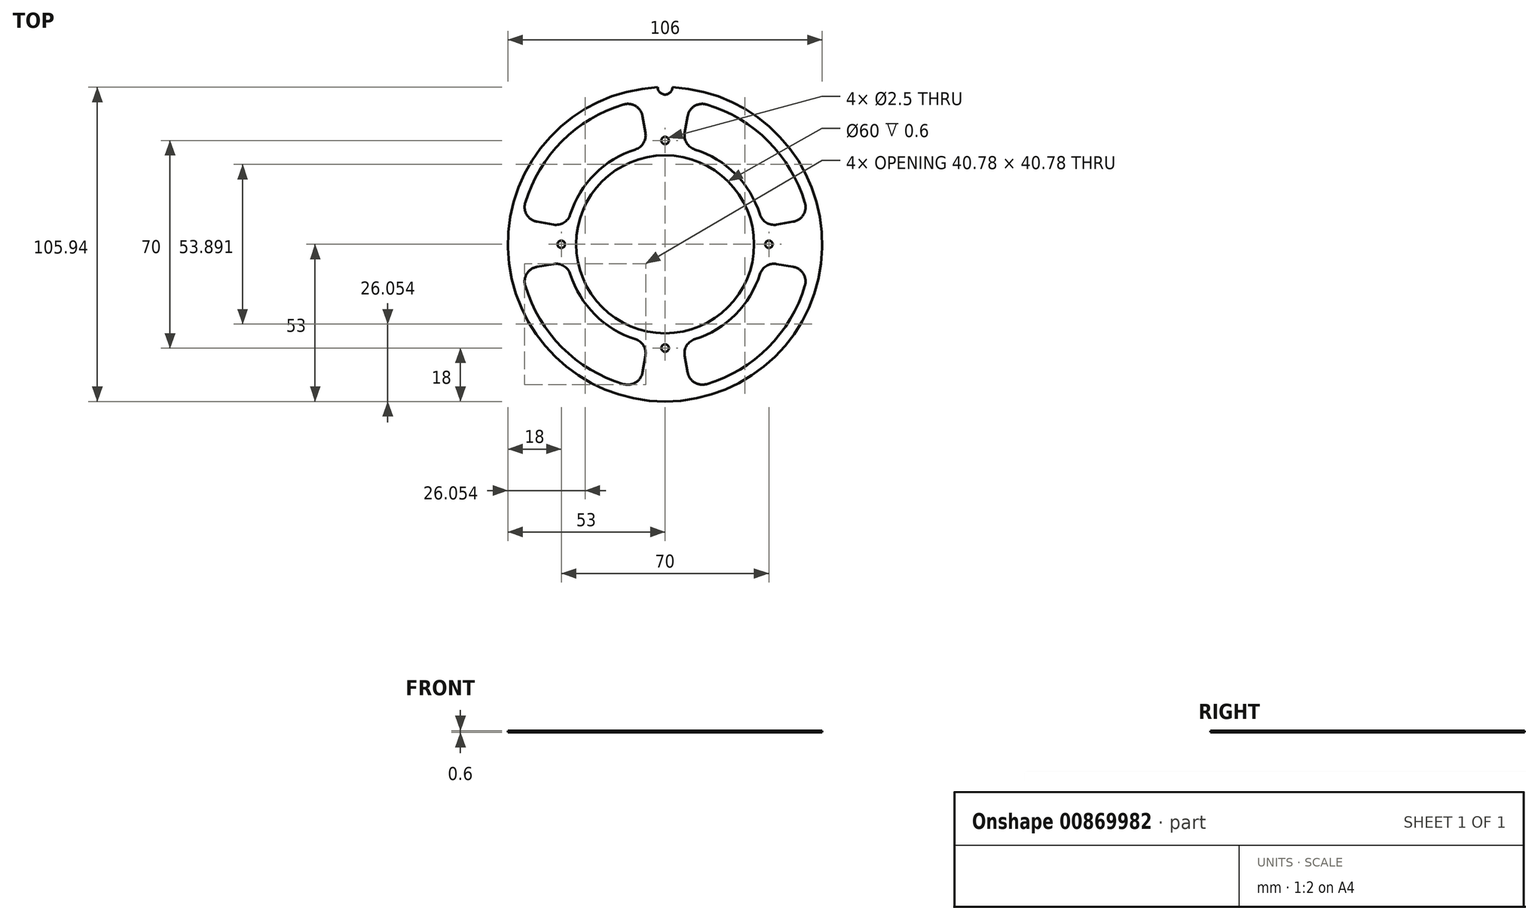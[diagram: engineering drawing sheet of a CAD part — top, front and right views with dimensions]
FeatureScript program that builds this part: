
annotation { "Feature Type Name" : "Feature", "Feature Type Description" : "" }
export const myFeature = defineFeature(function(context is Context, id is Id, definition is map)
    precondition{}
    {
        {
            var Q0;
            Q0=qCreatedBy(makeId("Top.planeOp"),FACE);
            var sketch = newSketch(context, id + "F0", { "sketchPlane" : qUnion([Q0])});
            skCircle(sketch, "E0", {"center": v(0, 0) * mm, "radius": 30 * mm});
            skCircle(sketch, "E1", {"center": v(0, 0) * mm, "radius": 53 * mm});
            skSolve(sketch);
        }
        {
            var Q0;
            Q0=makeQuery(id+"F0.imprint","IMPRINT",FACE,{"disambiguationData":[TD([[makeQuery(id+"F0.imprint","IMPRINT",EDGE,{"derivedFrom":sQuery(id+"F0.wireOp",EDGE,"E0")}),-1.0]])]});
            extrude(context, id + "F1", {"entities" : qUnion([Q0]), "depth" : 0.6 * mm, "offsetDistance" : 25 * mm});
        }
        {
            var Q0;
            Q0=makeQuery(id+"F1.opExtrude","CAP_FACE",FACE,{"disambiguationData":[OSD([sQuery(id+"F0.wireOp",EDGE,"E0"),sQuery(id+"F0.wireOp",EDGE,"E1")])],"isStart":false});
            var sketch = newSketch(context, id + "F2", { "sketchPlane" : qUnion([Q0])});
            skCircle(sketch, "E2", {"center": v(0, 35) * mm, "radius": 1.25 * mm});
            skCircle(sketch, "E3.1.0", {"center": v(-35, 0) * mm, "radius": 1.25 * mm});
            skCircle(sketch, "E3.2.0", {"center": v(0, -35) * mm, "radius": 1.25 * mm});
            skCircle(sketch, "E3.3.0", {"center": v(35, 0) * mm, "radius": 1.25 * mm});
            skPoint(sketch, "E3.center", {"position": v(0, 0) * mm});
            skSolve(sketch);
        }
        {
            var Q0;
            Q0=makeQuery(id+"F2.imprint","IMPRINT",FACE,{"disambiguationData":[TD([[makeQuery(id+"F2.imprint","IMPRINT",EDGE,{"derivedFrom":sQuery(id+"F2.wireOp",EDGE,"E2")}),1.0]])]});
            var Q1;
            Q1=makeQuery(id+"F2.imprint","IMPRINT",FACE,{"disambiguationData":[TD([[makeQuery(id+"F2.imprint","IMPRINT",EDGE,{"derivedFrom":sQuery(id+"F2.wireOp",EDGE,"E3.3.0")}),1.0]])]});
            var Q2;
            Q2=makeQuery(id+"F2.imprint","IMPRINT",FACE,{"disambiguationData":[TD([[makeQuery(id+"F2.imprint","IMPRINT",EDGE,{"derivedFrom":sQuery(id+"F2.wireOp",EDGE,"E3.2.0")}),1.0]])]});
            var Q3;
            Q3=makeQuery(id+"F2.imprint","IMPRINT",FACE,{"disambiguationData":[TD([[makeQuery(id+"F2.imprint","IMPRINT",EDGE,{"derivedFrom":sQuery(id+"F2.wireOp",EDGE,"E3.1.0")}),1.0]])]});
            extrude(context, id + "F3", {"entities" : qUnion([Q0, Q1, Q2, Q3]), "operationType" : NewBodyOperationType.REMOVE, "oppositeDirection" : true, "depth" : 25 * mm, "offsetDistance" : 25 * mm});
        }
        {
            var Q0;
            Q0=makeQuery(id+"F1.opExtrude","CAP_FACE",FACE,{"disambiguationData":[OSD([sQuery(id+"F0.wireOp",EDGE,"E0"),sQuery(id+"F0.wireOp",EDGE,"E1")])],"isStart":false});
            var sketch = newSketch(context, id + "F4", { "sketchPlane" : qUnion([Q0])});
            skCircle(sketch, "E4", {"center": v(0, 53) * mm, "radius": 2.5 * mm});
            skSolve(sketch);
        }
        {
            var Q0;
            {var subQ0=sQuery(id+"F4.wireOp",EDGE,"E4");var subQ1=makeQuery(id+"F1.opExtrude","CAP_EDGE",EDGE,{"disambiguationData":[OSD([sQuery(id+"F0.wireOp",EDGE,"E1")])],"isStart":false});var subQ2=makeQuery(id+"F4.imprint","INTERSECT",VERTEX,{"disambiguationData":[OD(0.0)],"derivedFrom":[subQ1,subQ0]});Q0=makeQuery(id+"F4.imprint","IMPRINT",FACE,{"disambiguationData":[TD([[makeQuery(id+"F4.imprint","IMPRINT",EDGE,{"disambiguationData":[TD([[subQ2,-1.0]])],"derivedFrom":subQ0}),1.0]])]});}
            extrude(context, id + "F5", {"entities" : qUnion([Q0]), "operationType" : NewBodyOperationType.REMOVE, "oppositeDirection" : true, "depth" : 25 * mm, "offsetDistance" : 25 * mm});
        }
        {
            var Q0;
            Q0=makeQuery(id+"F1.opExtrude","CAP_FACE",FACE,{"disambiguationData":[OSD([sQuery(id+"F0.wireOp",EDGE,"E0"),sQuery(id+"F0.wireOp",EDGE,"E1")])],"isStart":false});
            var sketch = newSketch(context, id + "F6", { "sketchPlane" : qUnion([Q0])});
            skPoint(sketch, "E5.center", {"position": v(0, 0) * mm});
            skLineSegment(sketch, "E6", {"start": v(0, 0) * mm, "end": v(0, 66.57) * mm, "construction": true});
            skLineSegment(sketch, "E7", {"start": v(-37.6, 6.63) * mm, "end": v(-43.22, 7.62) * mm});
            skLineSegment(sketch, "E8.3.3.0", {"start": v(-6.63, 37.6) * mm, "end": v(-7.62, 43.22) * mm});
            skArc(sketch, "E9.trimOffspring", {"start": v(-10.06, 31.97) * mm, "mid": v(-23.7, 23.7) * mm, "end": v(-31.97, 10.06) * mm});
            skArc(sketch, "E10.trimOffspring", {"start": v(-13.96, 47.14) * mm, "mid": v(-34.77, 34.77) * mm, "end": v(-47.14, 13.96) * mm});
            skPoint(sketch, "E11.visualSharp", {"position": v(-48.42, 8.54) * mm});
            skArc(sketch, "E11.filletArc", {"start": v(-47.14, 13.96) * mm, "mid": v(-46.6, 9.91) * mm, "end": v(-43.22, 7.62) * mm});
            skPoint(sketch, "E12.visualSharp", {"position": v(-33, 5.82) * mm});
            skArc(sketch, "E12.filletArc", {"start": v(-37.6, 6.63) * mm, "mid": v(-34.15, 7.28) * mm, "end": v(-31.97, 10.06) * mm});
            skPoint(sketch, "E13.visualSharp", {"position": v(-5.82, 33) * mm});
            skArc(sketch, "E13.filletArc", {"start": v(-10.06, 31.97) * mm, "mid": v(-7.28, 34.15) * mm, "end": v(-6.63, 37.6) * mm});
            skPoint(sketch, "E14.visualSharp", {"position": v(-8.54, 48.42) * mm});
            skArc(sketch, "E14.filletArc", {"start": v(-7.62, 43.22) * mm, "mid": v(-9.91, 46.6) * mm, "end": v(-13.96, 47.14) * mm});
            skArc(sketch, "E15.1.0", {"start": v(-31.97, -10.06) * mm, "mid": v(-23.7, -23.7) * mm, "end": v(-10.06, -31.97) * mm});
            skPoint(sketch, "E15.1.1", {"position": v(-48.42, -8.54) * mm});
            skLineSegment(sketch, "E15.1.2", {"start": v(-6.63, -37.6) * mm, "end": v(-7.62, -43.22) * mm});
            skArc(sketch, "E15.1.3", {"start": v(-31.97, -10.06) * mm, "mid": v(-34.15, -7.28) * mm, "end": v(-37.6, -6.63) * mm});
            skArc(sketch, "E15.1.4", {"start": v(-13.96, -47.14) * mm, "mid": v(-9.91, -46.6) * mm, "end": v(-7.62, -43.22) * mm});
            skPoint(sketch, "E15.1.5", {"position": v(-5.82, -33) * mm});
            skPoint(sketch, "E15.1.6", {"position": v(-8.54, -48.42) * mm});
            skArc(sketch, "E15.1.7", {"start": v(-47.14, -13.96) * mm, "mid": v(-34.77, -34.77) * mm, "end": v(-13.96, -47.14) * mm});
            skPoint(sketch, "E15.1.8", {"position": v(-33, -5.82) * mm});
            skLineSegment(sketch, "E15.1.9", {"start": v(-37.6, -6.63) * mm, "end": v(-43.22, -7.62) * mm});
            skArc(sketch, "E15.1.10", {"start": v(-6.63, -37.6) * mm, "mid": v(-7.28, -34.15) * mm, "end": v(-10.06, -31.97) * mm});
            skArc(sketch, "E15.1.11", {"start": v(-43.22, -7.62) * mm, "mid": v(-46.6, -9.91) * mm, "end": v(-47.14, -13.96) * mm});
            skArc(sketch, "E15.2.0", {"start": v(10.06, -31.97) * mm, "mid": v(23.7, -23.7) * mm, "end": v(31.97, -10.06) * mm});
            skPoint(sketch, "E15.2.1", {"position": v(8.54, -48.42) * mm});
            skLineSegment(sketch, "E15.2.2", {"start": v(37.6, -6.63) * mm, "end": v(43.22, -7.62) * mm});
            skArc(sketch, "E15.2.3", {"start": v(10.06, -31.97) * mm, "mid": v(7.28, -34.15) * mm, "end": v(6.63, -37.6) * mm});
            skArc(sketch, "E15.2.4", {"start": v(47.14, -13.96) * mm, "mid": v(46.6, -9.91) * mm, "end": v(43.22, -7.62) * mm});
            skPoint(sketch, "E15.2.5", {"position": v(33, -5.82) * mm});
            skPoint(sketch, "E15.2.6", {"position": v(48.42, -8.54) * mm});
            skArc(sketch, "E15.2.7", {"start": v(13.96, -47.14) * mm, "mid": v(34.77, -34.77) * mm, "end": v(47.14, -13.96) * mm});
            skPoint(sketch, "E15.2.8", {"position": v(5.82, -33) * mm});
            skLineSegment(sketch, "E15.2.9", {"start": v(6.63, -37.6) * mm, "end": v(7.62, -43.22) * mm});
            skArc(sketch, "E15.2.10", {"start": v(37.6, -6.63) * mm, "mid": v(34.15, -7.28) * mm, "end": v(31.97, -10.06) * mm});
            skArc(sketch, "E15.2.11", {"start": v(7.62, -43.22) * mm, "mid": v(9.91, -46.6) * mm, "end": v(13.96, -47.14) * mm});
            skPoint(sketch, "E16.0.3.0", {"position": v(8.54, 48.42) * mm});
            skPoint(sketch, "E16.4.3.0", {"position": v(48.42, 8.54) * mm});
            skLineSegment(sketch, "E16.5.3.0", {"start": v(6.63, 37.6) * mm, "end": v(7.62, 43.22) * mm});
            skArc(sketch, "E16.8.3.0", {"start": v(31.97, 10.06) * mm, "mid": v(34.15, 7.28) * mm, "end": v(37.6, 6.63) * mm});
            skArc(sketch, "E16.12.3.0", {"start": v(13.96, 47.14) * mm, "mid": v(9.91, 46.6) * mm, "end": v(7.62, 43.22) * mm});
            skPoint(sketch, "E16.16.3.0", {"position": v(5.82, 33) * mm});
            skArc(sketch, "E16.17.3.0", {"start": v(31.97, 10.06) * mm, "mid": v(23.7, 23.7) * mm, "end": v(10.06, 31.97) * mm});
            skArc(sketch, "E16.18.3.0", {"start": v(47.14, 13.96) * mm, "mid": v(34.77, 34.77) * mm, "end": v(13.96, 47.14) * mm});
            skPoint(sketch, "E16.22.3.0", {"position": v(33, 5.82) * mm});
            skLineSegment(sketch, "E16.23.3.0", {"start": v(37.6, 6.63) * mm, "end": v(43.22, 7.62) * mm});
            skArc(sketch, "E16.26.3.0", {"start": v(6.63, 37.6) * mm, "mid": v(7.28, 34.15) * mm, "end": v(10.06, 31.97) * mm});
            skArc(sketch, "E16.30.3.0", {"start": v(43.22, 7.62) * mm, "mid": v(46.6, 9.91) * mm, "end": v(47.14, 13.96) * mm});
            skSolve(sketch);
        }
        {
            var Q0;
            Q0=makeQuery(id+"F6.imprint","IMPRINT",FACE,{"disambiguationData":[TD([[makeQuery(id+"F6.imprint","IMPRINT",EDGE,{"derivedFrom":sQuery(id+"F6.wireOp",EDGE,"E7")}),-1.0]])]});
            var Q1;
            Q1=makeQuery(id+"F6.imprint","IMPRINT",FACE,{"disambiguationData":[TD([[makeQuery(id+"F6.imprint","IMPRINT",EDGE,{"derivedFrom":sQuery(id+"F6.wireOp",EDGE,"E16.5.3.0")}),-1.0]])]});
            var Q2;
            Q2=makeQuery(id+"F6.imprint","IMPRINT",FACE,{"disambiguationData":[TD([[makeQuery(id+"F6.imprint","IMPRINT",EDGE,{"derivedFrom":sQuery(id+"F6.wireOp",EDGE,"E15.2.0")}),-1.0]])]});
            var Q3;
            Q3=makeQuery(id+"F6.imprint","IMPRINT",FACE,{"disambiguationData":[TD([[makeQuery(id+"F6.imprint","IMPRINT",EDGE,{"derivedFrom":sQuery(id+"F6.wireOp",EDGE,"E15.1.0")}),-1.0]])]});
            extrude(context, id + "F7", {"entities" : qUnion([Q0, Q1, Q2, Q3]), "operationType" : NewBodyOperationType.REMOVE, "oppositeDirection" : true, "depth" : 2 * mm, "offsetDistance" : 25 * mm});
        }
    });
